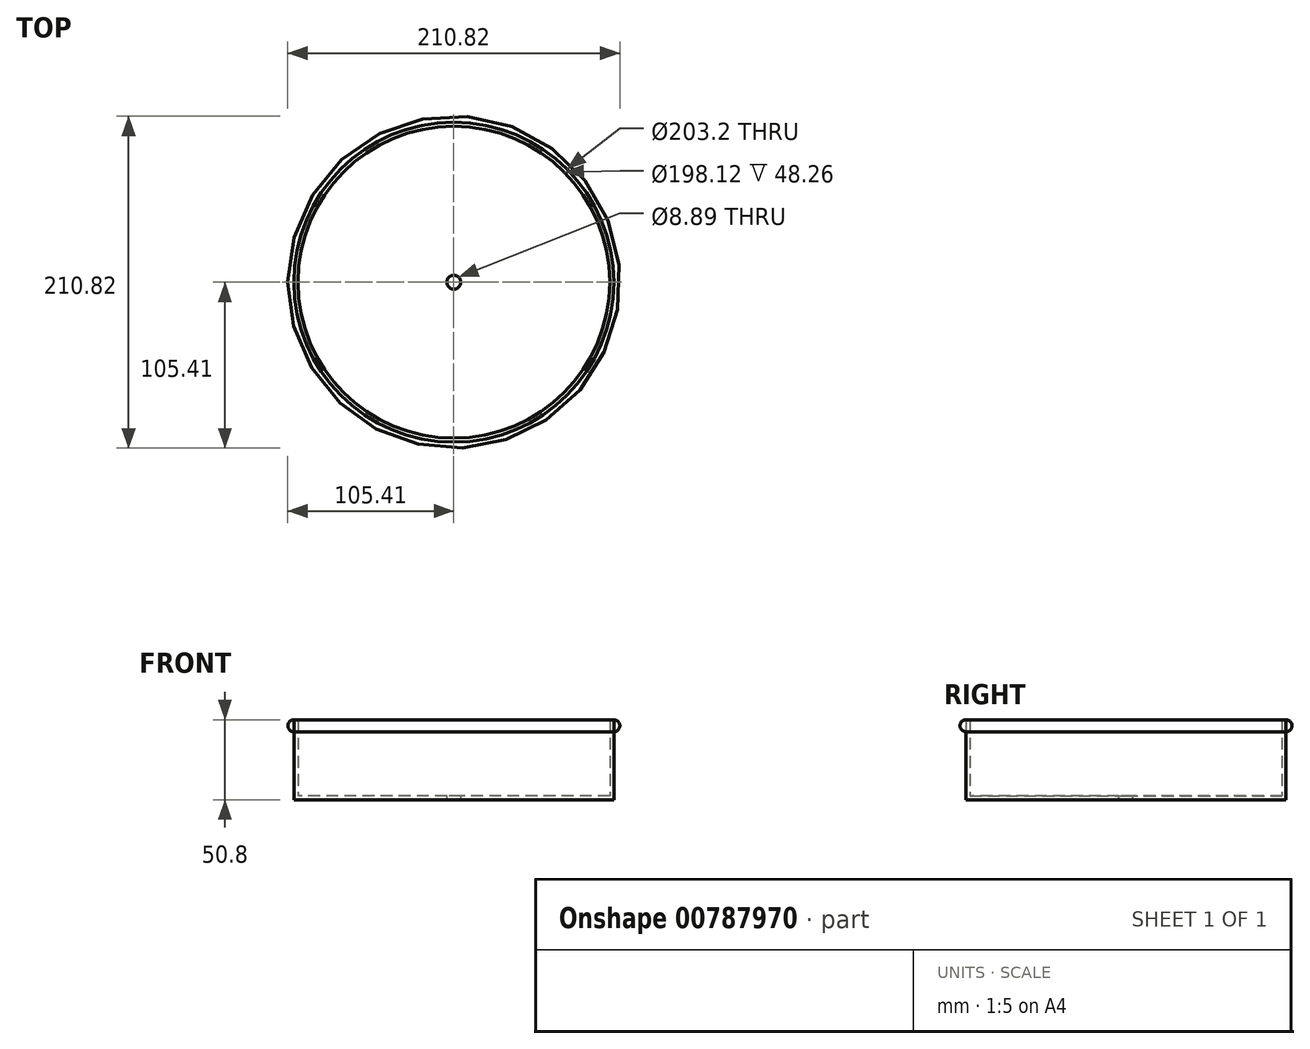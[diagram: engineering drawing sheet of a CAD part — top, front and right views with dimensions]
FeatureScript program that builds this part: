
annotation { "Feature Type Name" : "Feature", "Feature Type Description" : "" }
export const myFeature = defineFeature(function(context is Context, id is Id, definition is map)
    precondition{}
    {
        {
            var Q0;
            Q0=qCreatedBy(makeId("Top.planeOp"),FACE);
            var sketch = newSketch(context, id + "F0", { "sketchPlane" : qUnion([Q0])});
            skCircle(sketch, "E0", {"center": v(0, 0) * mm, "radius": 101.6 * mm});
            skSolve(sketch);
        }
        {
            var Q0;
            Q0=makeQuery(id+"F0.imprint","IMPRINT",FACE,{"disambiguationData":[TD([[makeQuery(id+"F0.imprint","IMPRINT",EDGE,{"derivedFrom":sQuery(id+"F0.wireOp",EDGE,"E0")}),1.0]])]});
            extrude(context, id + "F1", {"entities" : qUnion([Q0]), "depth" : 50.8 * mm, "offsetDistance" : 25.4 * mm});
        }
        {
            var Q0;
            Q0=makeQuery(id+"F1.opExtrude","CAP_FACE",FACE,{"disambiguationData":[OSD([sQuery(id+"F0.wireOp",EDGE,"E0")])],"isStart":false});
            shell(context, id + "F2", {"entities" : qUnion([Q0]), "thickness" : 2.54 * mm});
        }
        {
            var Q0;
            Q0=qCreatedBy(makeId("Front.planeOp"),FACE);
            var sketch = newSketch(context, id + "F3", { "sketchPlane" : qUnion([Q0])});
            skLineSegment(sketch, "E1.0", {"start": v(-101.6, 50.8) * mm, "end": v(0, 50.8) * mm});
            skLineSegment(sketch, "E2.0", {"start": v(-101.6, 0) * mm, "end": v(101.6, 0) * mm});
            skLineSegment(sketch, "E3", {"start": v(-101.6, 0) * mm, "end": v(-101.6, 50.8) * mm});
            skArc(sketch, "E4", {"start": v(101.6, 43.18) * mm, "mid": v(105.4, 47) * mm, "end": v(101.6, 50.8) * mm, "construction": true});
            skArc(sketch, "E5", {"start": v(101.6, 43.18) * mm, "mid": v(105.4, 47) * mm, "end": v(101.6, 50.8) * mm});
            skLineSegment(sketch, "E6", {"start": v(0, 0) * mm, "end": v(0, 50.8) * mm, "construction": true});
            skLineSegment(sketch, "E7", {"start": v(101.6, 43.18) * mm, "end": v(101.6, 50.8) * mm});
            skSolve(sketch);
        }
        {
            var Q0;
            Q0 = qSketchRegion(id + "F3", true);
            var Q1;
            Q1=sQuery(id+"F3.wireOp",EDGE,"E6");
            revolve(context, id + "F4", {"surfaceOperationType" : NewSurfaceOperationType.NEW, "entities" : qUnion([Q0]), "axis" : qUnion([Q1]), "revolveType" : RevolveType.FULL});
        }
        {
            var Q0;
            {var subQ0=sQuery(id+"F0.wireOp",EDGE,"E0");Q0=makeQuery(id+"F2.opShell","OFFSET_FACE",FACE,{"disambiguationData":[OSD([subQ0]),TDD([makeQuery(id+"F1.opExtrude","CAP_FACE",FACE,{"disambiguationData":[OSD([subQ0])],"isStart":true})])]});}
            var sketch = newSketch(context, id + "F5", { "sketchPlane" : qUnion([Q0])});
            skPoint(sketch, "E8", {"position": v(0, 0) * mm});
            skSolve(sketch);
        }
        {
            var Q0;
            Q0=sQuery(id+"F5.wireOp",VERTEX,"E8");
            var Q1;
            Q1=makeQuery(id+"F1.opExtrude","SWEPT_BODY",BODY,{"disambiguationData":[OSD([sQuery(id+"F0.wireOp",EDGE,"E0")])]});
            hole(context, id + "F6", {"style" : HoleStyle.SIMPLE, "endStyle" : HoleEndStyle.THROUGH, "holeDiameter" : 8.9 * mm, "majorDiameter" : 6.35 * mm, "isTappedThrough" : true, "tappedDepth" : 12.7 * mm, "tapClearance" : 3, "locations" : qUnion([Q0]), "scope" : qUnion([Q1])});
        }
    });
